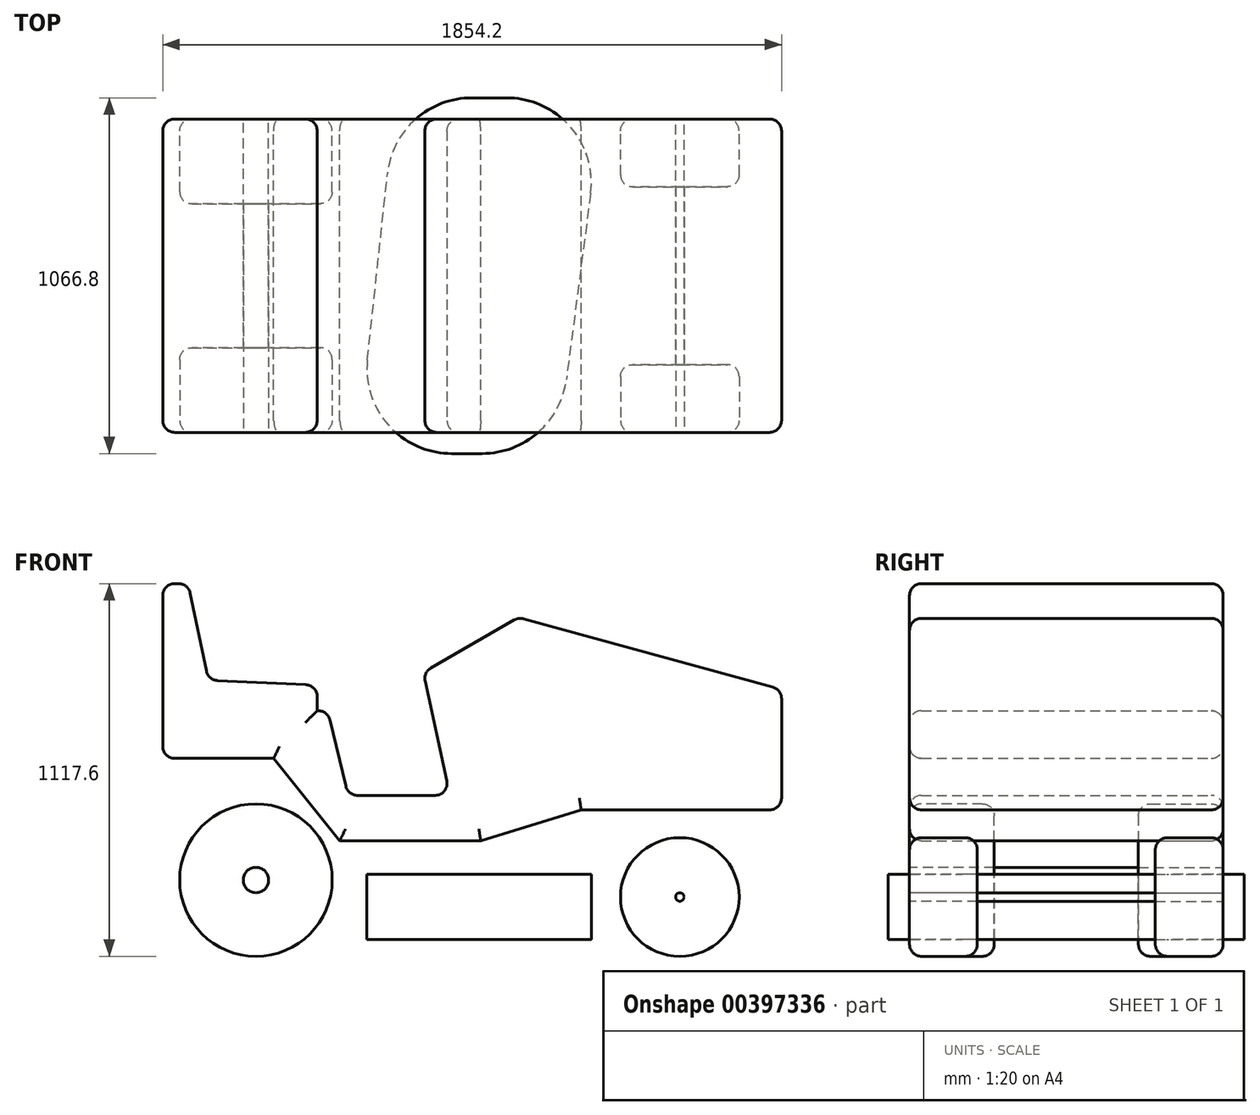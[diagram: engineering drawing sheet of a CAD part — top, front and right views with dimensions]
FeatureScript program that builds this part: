
annotation { "Feature Type Name" : "Feature", "Feature Type Description" : "" }
export const myFeature = defineFeature(function(context is Context, id is Id, definition is map)
    precondition{}
    {
        {
            var Q0;
            Q0=qCreatedBy(makeId("Front.planeOp"),FACE);
            var sketch = newSketch(context, id + "F0", { "sketchPlane" : qUnion([Q0])});
            skLineSegment(sketch, "E0", {"start": v(847.45, 439.14) * mm, "end": v(847.45, 800.1) * mm});
            skLineSegment(sketch, "E1", {"start": v(847.45, 800.1) * mm, "end": v(60.05, 1016) * mm});
            skLineSegment(sketch, "E2", {"start": v(60.05, 1016) * mm, "end": v(-225.9, 850.9) * mm});
            skLineSegment(sketch, "E3", {"start": v(-225.9, 850.9) * mm, "end": v(-146.3, 482.6) * mm});
            skLineSegment(sketch, "E4", {"start": v(-146.3, 482.6) * mm, "end": v(-451.1, 482.6) * mm});
            skLineSegment(sketch, "E5", {"start": v(-451.1, 482.6) * mm, "end": v(-512.88, 736.6) * mm});
            skLineSegment(sketch, "E6", {"start": v(-512.88, 736.6) * mm, "end": v(-543.76, 736.6) * mm});
            skLineSegment(sketch, "E7", {"start": v(-543.76, 736.6) * mm, "end": v(-543.76, 812.8) * mm});
            skLineSegment(sketch, "E8", {"start": v(-543.76, 812.8) * mm, "end": v(-869.83, 828.1) * mm});
            skLineSegment(sketch, "E9", {"start": v(-869.83, 828.1) * mm, "end": v(-930.55, 1117.6) * mm});
            skLineSegment(sketch, "E10", {"start": v(-930.55, 1117.6) * mm, "end": v(-1006.75, 1117.6) * mm});
            skLineSegment(sketch, "E11", {"start": v(-1006.75, 1117.6) * mm, "end": v(-1006.75, 593.54) * mm});
            skCircle(sketch, "E12", {"center": v(542.65, 177.8) * mm, "radius": 177.8 * mm, "construction": true});
            skCircle(sketch, "E13", {"center": v(-727.35, 228.6) * mm, "radius": 228.6 * mm, "construction": true});
            skLineSegment(sketch, "E14", {"start": v(-727.35, 0) * mm, "end": v(542.65, 0) * mm, "construction": true});
            skLineSegment(sketch, "E15", {"start": v(847.45, 439.14) * mm, "end": v(247.16, 439.14) * mm});
            skLineSegment(sketch, "E16", {"start": v(247.16, 439.14) * mm, "end": v(-53.91, 346.5) * mm});
            skLineSegment(sketch, "E17", {"start": v(-53.91, 346.5) * mm, "end": v(-475.93, 346.5) * mm});
            skLineSegment(sketch, "E18", {"start": v(-475.93, 346.5) * mm, "end": v(-674.07, 593.54) * mm});
            skLineSegment(sketch, "E19", {"start": v(-674.07, 593.54) * mm, "end": v(-1006.75, 593.54) * mm});
            skPoint(sketch, "E20.start.orphan", {"position": v(-1006.75, 228.6) * mm});
            skPoint(sketch, "E21.orphan", {"position": v(847.45, 228.6) * mm});
            skSolve(sketch);
        }
        {
            var Q0;
            Q0 = qSketchRegion(id + "F0", true);
            extrude(context, id + "F1", {"entities" : qUnion([Q0]), "endBound" : BoundingType.SYMMETRIC, "depth" : 939.8 * mm});
        }
        {
            var Q0;
            Q0=qCreatedBy(makeId("Front.planeOp"),FACE);
            var sketch = newSketch(context, id + "F2", { "sketchPlane" : qUnion([Q0])});
            skCircle(sketch, "E22", {"center": v(-727.35, 228.6) * mm, "radius": 38.1 * mm});
            skCircle(sketch, "E23", {"center": v(542.65, 177.8) * mm, "radius": 12.7 * mm});
            skSolve(sketch);
        }
        {
            var Q0;
            Q0 = qSketchRegion(id + "F2", true);
            extrude(context, id + "F3", {"entities" : qUnion([Q0]), "endBound" : BoundingType.SYMMETRIC, "depth" : 939.8 * mm});
        }
        {
            var Q0;
            Q0=makeQuery(id+"F3.opExtrude","CAP_FACE",FACE,{"disambiguationData":[OSD([sQuery(id+"F2.wireOp",EDGE,"E22")])],"isStart":false});
            var sketch = newSketch(context, id + "F4", { "sketchPlane" : qUnion([Q0])});
            skCircle(sketch, "E24.0", {"center": v(-727.35, 228.6) * mm, "radius": 228.6 * mm});
            skSolve(sketch);
        }
        {
            var Q0;
            Q0 = qSketchRegion(id + "F4", true);
            extrude(context, id + "F5", {"entities" : qUnion([Q0]), "operationType" : NewBodyOperationType.ADD, "oppositeDirection" : true, "depth" : 254 * mm});
        }
        {
            var Q0;
            Q0=makeQuery(id+"F3.opExtrude","CAP_FACE",FACE,{"disambiguationData":[OSD([sQuery(id+"F2.wireOp",EDGE,"E23")])],"isStart":false});
            var sketch = newSketch(context, id + "F6", { "sketchPlane" : qUnion([Q0])});
            skCircle(sketch, "E25.0", {"center": v(542.65, 177.8) * mm, "radius": 177.8 * mm});
            skSolve(sketch);
        }
        {
            var Q0;
            Q0 = qSketchRegion(id + "F6", true);
            extrude(context, id + "F7", {"entities" : qUnion([Q0]), "operationType" : NewBodyOperationType.ADD, "oppositeDirection" : true, "depth" : 203.2 * mm});
        }
        {
            var Q0;
            Q0=makeQuery(id+"F3.opExtrude","SWEPT_BODY",BODY,{"disambiguationData":[OSD([sQuery(id+"F2.wireOp",EDGE,"E22")])]});
            var Q1;
            Q1=makeQuery(id+"F3.opExtrude","SWEPT_BODY",BODY,{"disambiguationData":[OSD([sQuery(id+"F2.wireOp",EDGE,"E23")])]});
            var Q2;
            Q2=qCreatedBy(makeId("Front.planeOp"),FACE);
            mirror(context, id + "F8", {"operationType" : NewBodyOperationType.ADD, "entities" : qUnion([Q0, Q1]), "mirrorPlane" : qUnion([Q2])});
        }
        {
            var Q0;
            Q0=makeQuery(id+"F1.opExtrude","CAP_FACE",FACE,{"disambiguationData":[OSD([sQuery(id+"F0.wireOp",EDGE,"E20"),sQuery(id+"F0.wireOp",EDGE,"E0"),sQuery(id+"F0.wireOp",EDGE,"E1"),sQuery(id+"F0.wireOp",EDGE,"E2"),sQuery(id+"F0.wireOp",EDGE,"E3"),sQuery(id+"F0.wireOp",EDGE,"E4"),sQuery(id+"F0.wireOp",EDGE,"E5"),sQuery(id+"F0.wireOp",EDGE,"E6"),sQuery(id+"F0.wireOp",EDGE,"E7"),sQuery(id+"F0.wireOp",EDGE,"E8"),sQuery(id+"F0.wireOp",EDGE,"E9"),sQuery(id+"F0.wireOp",EDGE,"E10"),sQuery(id+"F0.wireOp",EDGE,"E11")])],"isStart":false});
            var Q1;
            Q1=makeQuery(id+"F1.opExtrude","CAP_FACE",FACE,{"disambiguationData":[OSD([sQuery(id+"F0.wireOp",EDGE,"E20"),sQuery(id+"F0.wireOp",EDGE,"E0"),sQuery(id+"F0.wireOp",EDGE,"E1"),sQuery(id+"F0.wireOp",EDGE,"E2"),sQuery(id+"F0.wireOp",EDGE,"E3"),sQuery(id+"F0.wireOp",EDGE,"E4"),sQuery(id+"F0.wireOp",EDGE,"E5"),sQuery(id+"F0.wireOp",EDGE,"E6"),sQuery(id+"F0.wireOp",EDGE,"E7"),sQuery(id+"F0.wireOp",EDGE,"E8"),sQuery(id+"F0.wireOp",EDGE,"E9"),sQuery(id+"F0.wireOp",EDGE,"E10"),sQuery(id+"F0.wireOp",EDGE,"E11")])],"isStart":true});
            var Q2;
            Q2=makeQuery(id+"F1.opExtrude","SWEPT_FACE",FACE,{"disambiguationData":[OSD([sQuery(id+"F0.wireOp",EDGE,"E1")])]});
            var Q3;
            Q3=makeQuery(id+"F1.opExtrude","SWEPT_FACE",FACE,{"disambiguationData":[OSD([sQuery(id+"F0.wireOp",EDGE,"E0")])]});
            var Q4;
            Q4=makeQuery(id+"F1.opExtrude","SWEPT_FACE",FACE,{"disambiguationData":[OSD([sQuery(id+"F0.wireOp",EDGE,"E20")])]});
            var Q5;
            Q5=makeQuery(id+"F1.opExtrude","SWEPT_FACE",FACE,{"disambiguationData":[OSD([sQuery(id+"F0.wireOp",EDGE,"E2")])]});
            var Q6;
            Q6=makeQuery(id+"F1.opExtrude","SWEPT_FACE",FACE,{"disambiguationData":[OSD([sQuery(id+"F0.wireOp",EDGE,"E3")])]});
            var Q7;
            Q7=makeQuery(id+"F1.opExtrude","SWEPT_FACE",FACE,{"disambiguationData":[OSD([sQuery(id+"F0.wireOp",EDGE,"E4")])]});
            var Q8;
            Q8=makeQuery(id+"F1.opExtrude","SWEPT_FACE",FACE,{"disambiguationData":[OSD([sQuery(id+"F0.wireOp",EDGE,"E8")])]});
            var Q9;
            Q9=makeQuery(id+"F1.opExtrude","SWEPT_FACE",FACE,{"disambiguationData":[OSD([sQuery(id+"F0.wireOp",EDGE,"E9")])]});
            var Q10;
            Q10=makeQuery(id+"F1.opExtrude","SWEPT_FACE",FACE,{"disambiguationData":[OSD([sQuery(id+"F0.wireOp",EDGE,"E11")])]});
            var Q11;
            Q11=makeQuery(id+"F1.opExtrude","SWEPT_FACE",FACE,{"disambiguationData":[OSD([sQuery(id+"F0.wireOp",EDGE,"E5")])]});
            var Q12;
            Q12=makeQuery(id+"F5.opExtrude","SWEPT_FACE",FACE,{"disambiguationData":[OSD([sQuery(id+"F4.wireOp",EDGE,"E24.0")])]});
            var Q13;
            Q13=makeQuery(id+"F8.opPattern","COPY",FACE,{"derivedFrom":makeQuery(id+"F5.opExtrude","SWEPT_FACE",FACE,{"disambiguationData":[OSD([sQuery(id+"F4.wireOp",EDGE,"E24.0")])]}),"instanceName":"1"});
            var Q14;
            Q14=makeQuery(id+"F7.opExtrude","SWEPT_FACE",FACE,{"disambiguationData":[OSD([sQuery(id+"F6.wireOp",EDGE,"E25.0")])]});
            var Q15;
            Q15=makeQuery(id+"F8.opPattern","COPY",FACE,{"derivedFrom":makeQuery(id+"F7.opExtrude","SWEPT_FACE",FACE,{"disambiguationData":[OSD([sQuery(id+"F6.wireOp",EDGE,"E25.0")])]}),"instanceName":"1"});
            fillet(context, id + "F9", {"entities" : qUnion([Q0, Q1, Q2, Q3, Q4, Q5, Q6, Q7, Q8, Q9, Q10, Q11, Q12, Q13, Q14, Q15]), "radius" : 35.56 * mm, "tangentPropagation" : true, "allowEdgeOverflow" : false});
        }
        {
            var Q0;
            Q0=makeQuery(id+"F1.opExtrude","SWEPT_FACE",FACE,{"disambiguationData":[OSD([sQuery(id+"F0.wireOp",EDGE,"E11")])]});
            cPlane(context, id + "F10", {"entities" : qUnion([Q0]), "cplaneType" : CPlaneType.OFFSET, "offset" : 152.4 * mm, "width" : 152.4 * mm, "height" : 152.4 * mm});
        }
        {
            var Q0;
            Q0=qCreatedBy(id+"F10.planeOp",FACE);
            var sketch = newSketch(context, id + "F11", { "sketchPlane" : qUnion([Q0])});
            skCircle(sketch, "E26", {"center": v(711.2, 965.2) * mm, "radius": 82.55 * mm});
            skLineSegment(sketch, "E27", {"start": v(434.34, 0) * mm, "end": v(716.87, 0) * mm, "construction": true});
            skLineSegment(sketch, "E28", {"start": v(0, 593.54) * mm, "end": v(0, -239.28) * mm, "construction": true});
            skSolve(sketch);
        }
        {
            var Q0;
            Q0=qCreatedBy(makeId("Top.planeOp"),FACE);
            cPlane(context, id + "F12", {"entities" : qUnion([Q0]), "cplaneType" : CPlaneType.OFFSET, "offset" : 50.8 * mm, "width" : 152.4 * mm, "height" : 152.4 * mm});
        }
        {
            var Q0;
            Q0=qCreatedBy(id+"F12.planeOp",FACE);
            var sketch = newSketch(context, id + "F13", { "sketchPlane" : qUnion([Q0])});
            skLineSegment(sketch, "E29", {"start": v(-308.63, 533.4) * mm, "end": v(312.76, 533.4) * mm});
            skLineSegment(sketch, "E30", {"start": v(312.76, 533.4) * mm, "end": v(173.73, -533.4) * mm});
            skLineSegment(sketch, "E31", {"start": v(173.73, -533.4) * mm, "end": v(-423.6, -533.4) * mm});
            skLineSegment(sketch, "E32", {"start": v(-423.6, -533.4) * mm, "end": v(-308.63, 533.4) * mm});
            skLineSegment(sketch, "E33", {"start": v(0, 0) * mm, "end": v(364.96, 0) * mm, "construction": true});
            skSolve(sketch);
        }
        {
            var Q0;
            Q0 = qSketchRegion(id + "F13", true);
            extrude(context, id + "F14", {"entities" : qUnion([Q0]), "depth" : 195.58 * mm});
        }
        {
            var Q0;
            Q0=makeQuery(id+"F14.opExtrude","SWEPT_EDGE",EDGE,{"disambiguationData":[OSD([sQuery(id+"F13.wireOp",EDGE,"E30"),sQuery(id+"F13.wireOp",EDGE,"E31")])]});
            var Q1;
            Q1=makeQuery(id+"F14.opExtrude","SWEPT_EDGE",EDGE,{"disambiguationData":[OSD([sQuery(id+"F13.wireOp",EDGE,"E31"),sQuery(id+"F13.wireOp",EDGE,"E32")])]});
            var Q2;
            Q2=makeQuery(id+"F14.opExtrude","SWEPT_EDGE",EDGE,{"disambiguationData":[OSD([sQuery(id+"F13.wireOp",EDGE,"E29"),sQuery(id+"F13.wireOp",EDGE,"E30")])]});
            var Q3;
            Q3=makeQuery(id+"F14.opExtrude","SWEPT_EDGE",EDGE,{"disambiguationData":[OSD([sQuery(id+"F13.wireOp",EDGE,"E29"),sQuery(id+"F13.wireOp",EDGE,"E32")])]});
            fillet(context, id + "F15", {"entities" : qUnion([Q0, Q1, Q2, Q3]), "radius" : 254 * mm, "tangentPropagation" : true, "allowEdgeOverflow" : false});
        }
    });
